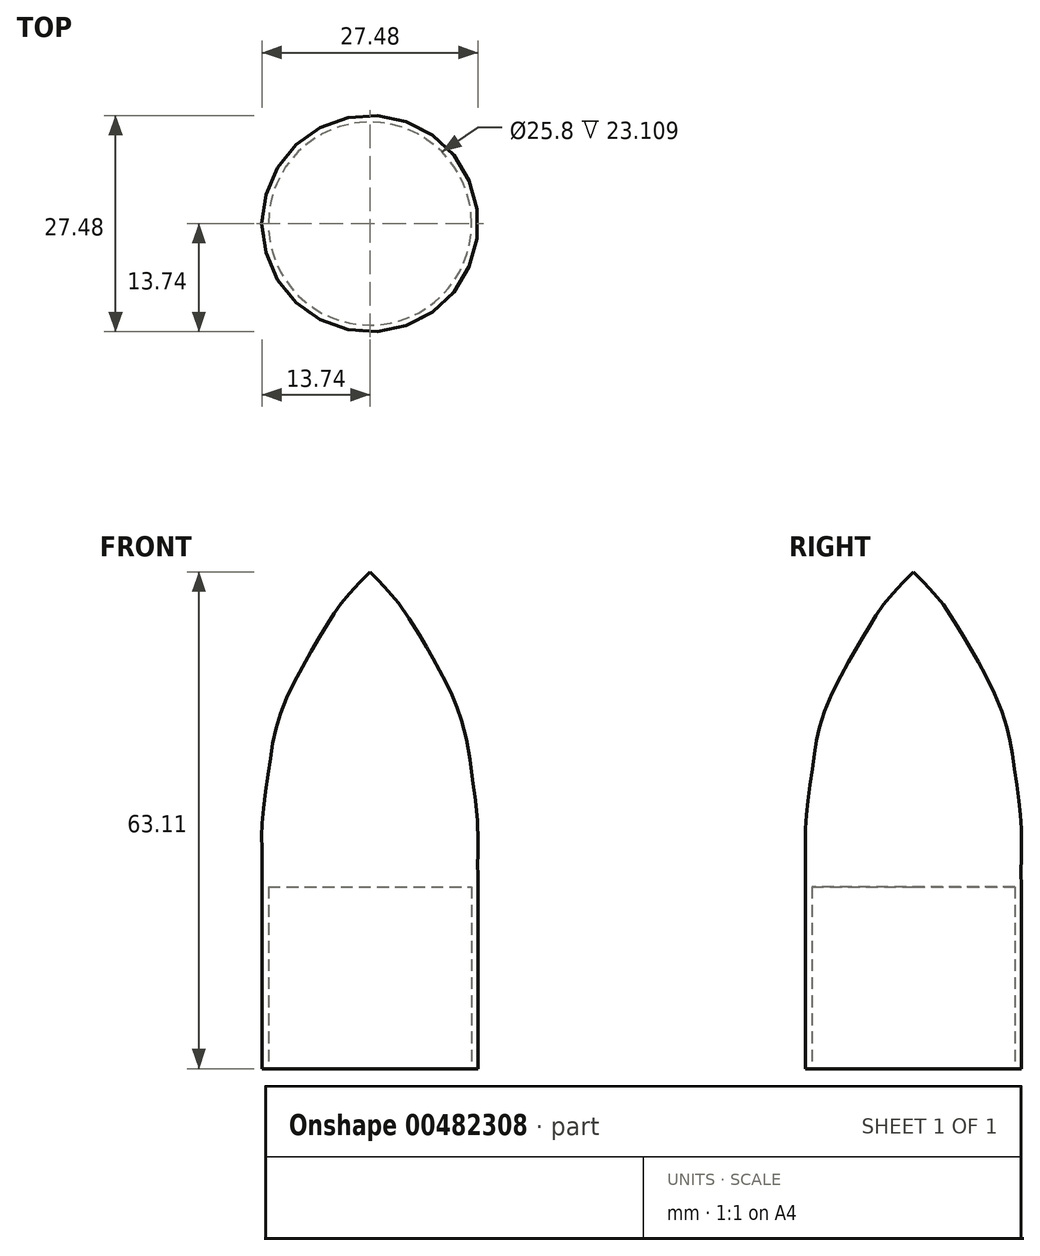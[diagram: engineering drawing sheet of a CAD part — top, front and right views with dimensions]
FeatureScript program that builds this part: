
annotation { "Feature Type Name" : "Feature", "Feature Type Description" : "" }
export const myFeature = defineFeature(function(context is Context, id is Id, definition is map)
    precondition{}
    {
        {
            var Q0;
            Q0=qCreatedBy(makeId("Front.planeOp"),FACE);
            var sketch = newSketch(context, id + "F0", { "sketchPlane" : qUnion([Q0])});
            skLineSegment(sketch, "E0", {"start": v(-12.9, 0) * mm, "end": v(-13.7, 0) * mm});
            skLineSegment(sketch, "E1", {"start": v(-13.7, 0) * mm, "end": v(-13.7, 23.1) * mm});
            skLineSegment(sketch, "E2", {"start": v(-13.7, 23.1) * mm, "end": v(-12.9, 23.1) * mm});
            skLineSegment(sketch, "E3", {"start": v(-12.9, 23.1) * mm, "end": v(-12.9, 0) * mm});
            skLineSegment(sketch, "E4", {"start": v(-12.9, 23.1) * mm, "end": v(0, 23.1) * mm});
            skLineSegment(sketch, "E5", {"start": v(0, 23.1) * mm, "end": v(0, 63.1) * mm});
            skFitSpline(sketch, "E6", {"points": [v(-13.7, 23.1) * mm, v(-13.7, 27.3) * mm, v(-13.7, 31.01) * mm, v(-12.9, 37.67) * mm, v(-11.85, 43.54) * mm, v(-9.22, 49.89) * mm, v(-5.66, 56.08) * mm, v(-3.5, 59.33) * mm, v(0, 63.1) * mm], "startDerivative": vector(0.27, 39.44) * mm, "endDerivative": vector(31.3, 31.85) * mm});
            skLineSegment(sketch, "E7", {"start": v(0, 0) * mm, "end": v(0, 67.83) * mm});
            skSolve(sketch);
        }
        {
            var Q0;
            Q0=makeQuery(id+"F0.imprint","IMPRINT",FACE,{"disambiguationData":[TD([[makeQuery(id+"F0.imprint","IMPRINT",EDGE,{"derivedFrom":sQuery(id+"F0.wireOp",EDGE,"E2")}),1.0]])]});
            var Q1;
            Q1=makeQuery(id+"F0.imprint","IMPRINT",FACE,{"disambiguationData":[TD([[makeQuery(id+"F0.imprint","IMPRINT",EDGE,{"derivedFrom":sQuery(id+"F0.wireOp",EDGE,"E0")}),-1.0]])]});
            var Q2;
            Q2=sQuery(id+"F0.wireOp",EDGE,"E7");
            revolve(context, id + "F1", {"entities" : qUnion([Q0, Q1]), "axis" : qUnion([Q2]), "revolveType" : RevolveType.FULL});
        }
    });
